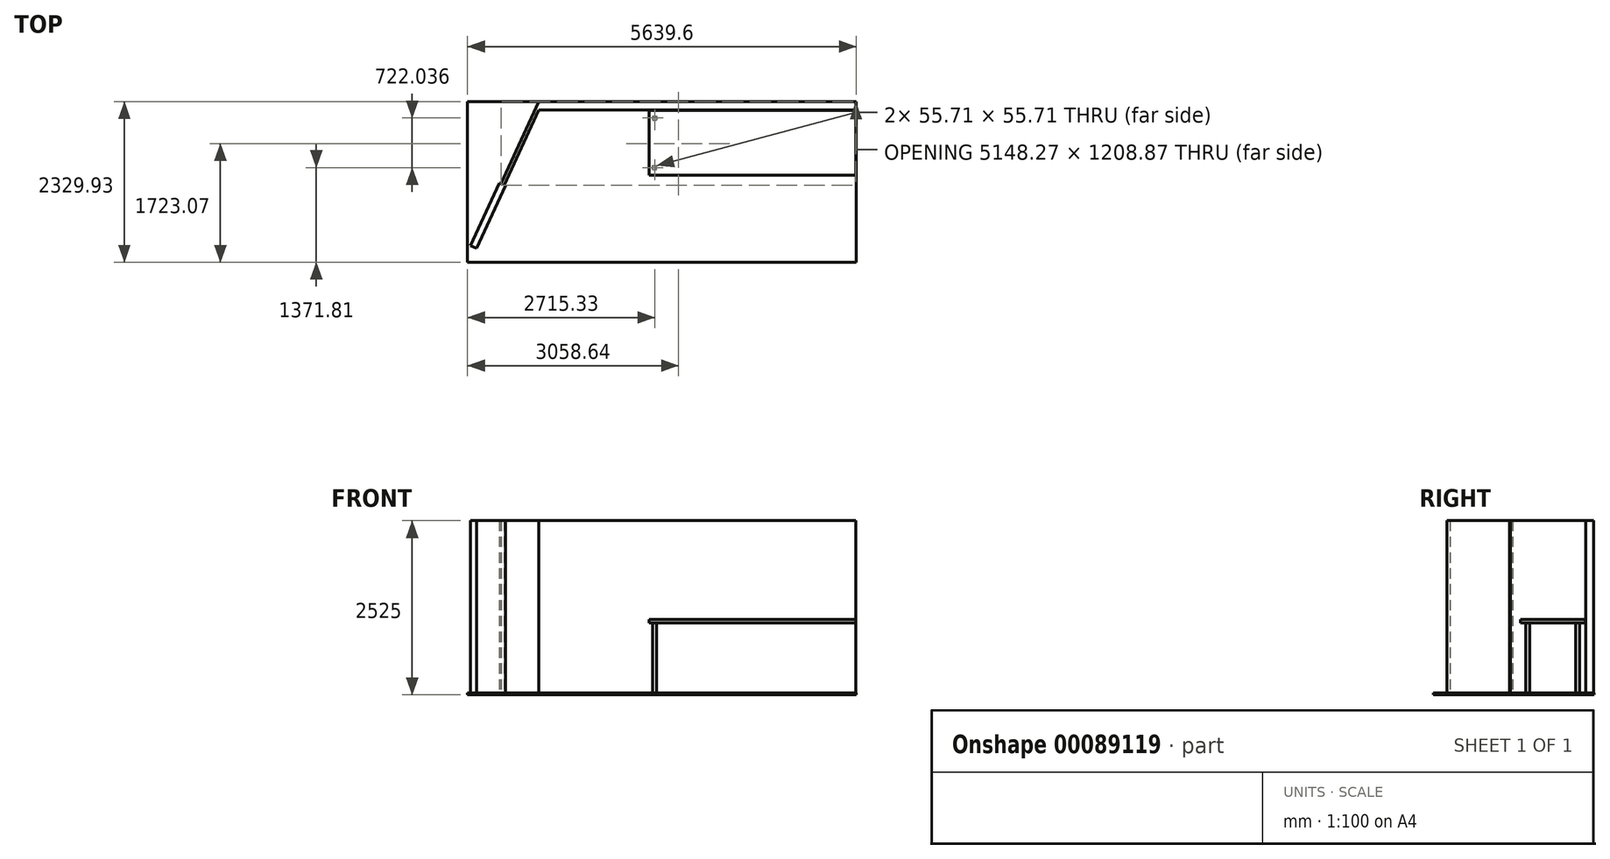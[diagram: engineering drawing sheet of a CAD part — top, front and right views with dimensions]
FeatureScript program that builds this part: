
annotation { "Feature Type Name" : "Feature", "Feature Type Description" : "" }
export const myFeature = defineFeature(function(context is Context, id is Id, definition is map)
    precondition{}
    {
        {
            var Q0;
            Q0=qCreatedBy(makeId("Top.planeOp"),FACE);
            var sketch = newSketch(context, id + "F0", { "sketchPlane" : qUnion([Q0])});
            skLineSegment(sketch, "E0.bottom", {"start": v(-637.71, 864.23) * mm, "end": v(2362.29, 864.23) * mm, "construction": true});
            skLineSegment(sketch, "E0.top", {"start": v(-637.71, -85.77) * mm, "end": v(2362.29, -85.77) * mm, "construction": true});
            skLineSegment(sketch, "E0.left", {"start": v(-637.71, 864.23) * mm, "end": v(-637.71, -85.77) * mm, "construction": true});
            skLineSegment(sketch, "E0.right", {"start": v(2362.29, 864.23) * mm, "end": v(2362.29, -85.77) * mm, "construction": true});
            skLineSegment(sketch, "E1", {"start": v(-637.71, 864.23) * mm, "end": v(-2237.71, 864.23) * mm});
            skLineSegment(sketch, "E2", {"start": v(-2237.71, 864.23) * mm, "end": v(-2740.58, -225.32) * mm});
            skLineSegment(sketch, "E3", {"start": v(-2740.58, -225.32) * mm, "end": v(-2785.98, -204.37) * mm});
            skLineSegment(sketch, "E4", {"start": v(-2785.98, -204.37) * mm, "end": v(-2237.71, 983.55) * mm});
            skLineSegment(sketch, "E5", {"start": v(-2237.71, 983.55) * mm, "end": v(2362.29, 983.55) * mm});
            skLineSegment(sketch, "E6", {"start": v(2362.29, 983.55) * mm, "end": v(2362.29, 864.23) * mm});
            skLineSegment(sketch, "E7", {"start": v(-2237.71, 864.23) * mm, "end": v(-2237.71, -45.77) * mm, "construction": true});
            skLineSegment(sketch, "E8", {"start": v(-2237.71, -45.77) * mm, "end": v(-2657.71, -45.77) * mm, "construction": true});
            skLineSegment(sketch, "E9", {"start": v(-2237.71, 864.23) * mm, "end": v(-2237.71, 1303.18) * mm, "construction": true});
            skLineSegment(sketch, "E10", {"start": v(-637.71, 864.23) * mm, "end": v(2362.29, 864.23) * mm});
            skLineSegment(sketch, "E11.bottom", {"start": v(-2740.58, -225.32) * mm, "end": v(-2808.68, -193.9) * mm});
            skLineSegment(sketch, "E11.top", {"start": v(-3136.94, -1143.76) * mm, "end": v(-3227.74, -1101.85) * mm});
            skLineSegment(sketch, "E11.left", {"start": v(-2717.88, -235.8) * mm, "end": v(-3136.94, -1143.76) * mm});
            skLineSegment(sketch, "E11.right", {"start": v(-2808.68, -193.9) * mm, "end": v(-3227.74, -1101.85) * mm});
            skLineSegment(sketch, "E12", {"start": v(-2740.58, -225.32) * mm, "end": v(-2717.88, -235.8) * mm});
            skSolve(sketch);
        }
        {
            var Q0;
            Q0=makeQuery(id+"F0.imprint","IMPRINT",FACE,{"disambiguationData":[TD([[makeQuery(id+"F0.imprint","IMPRINT",EDGE,{"derivedFrom":sQuery(id+"F0.wireOp",EDGE,"E1")}),-1.0]])]});
            var Q1;
            Q1=makeQuery(id+"F0.imprint","IMPRINT",FACE,{"disambiguationData":[TD([[makeQuery(id+"F0.imprint","IMPRINT",EDGE,{"derivedFrom":sQuery(id+"F0.wireOp",EDGE,"E11.top")}),-1.0]])]});
            extrude(context, id + "F1", {"entities" : qUnion([Q0, Q1]), "depth" : 2500 * mm});
        }
        {
            var Q0;
            Q0=makeQuery(id+"F1.opExtrude","CAP_FACE",FACE,{"disambiguationData":[OSD([sQuery(id+"F0.wireOp",EDGE,"E1"),sQuery(id+"F0.wireOp",EDGE,"E2"),sQuery(id+"F0.wireOp",EDGE,"E3"),sQuery(id+"F0.wireOp",EDGE,"E4"),sQuery(id+"F0.wireOp",EDGE,"E5"),sQuery(id+"F0.wireOp",EDGE,"E6"),sQuery(id+"F0.wireOp",EDGE,"E10")])],"isStart":true});
            cPlane(context, id + "F2", {"entities" : qUnion([Q0]), "cplaneType" : CPlaneType.OFFSET, "offset" : 1065 * mm, "oppositeDirection" : true, "width" : 150 * mm, "height" : 150 * mm});
        }
        {
            var Q0;
            Q0=qCreatedBy(id+"F2.planeOp",FACE);
            var sketch = newSketch(context, id + "F3", { "sketchPlane" : qUnion([Q0])});
            skLineSegment(sketch, "E13.bottom", {"start": v(-636.4, 81.22) * mm, "end": v(2359.83, 81.22) * mm});
            skLineSegment(sketch, "E13.top", {"start": v(-636.4, -858.96) * mm, "end": v(2359.83, -858.96) * mm});
            skLineSegment(sketch, "E13.left", {"start": v(-636.4, 81.22) * mm, "end": v(-636.4, -858.96) * mm});
            skLineSegment(sketch, "E13.right", {"start": v(2359.83, 81.22) * mm, "end": v(2359.83, -858.96) * mm});
            skSolve(sketch);
        }
        {
            var Q0;
            Q0=makeQuery(id+"F3.imprint","IMPRINT",FACE,{"disambiguationData":[TD([[makeQuery(id+"F3.imprint","IMPRINT",EDGE,{"derivedFrom":sQuery(id+"F3.wireOp",EDGE,"E13.bottom")}),-1.0]])]});
            extrude(context, id + "F4", {"entities" : qUnion([Q0]), "depth" : 45 * mm});
        }
        {
            var Q0;
            Q0=makeQuery(id+"F0.imprint","IMPRINT",FACE,{"disambiguationData":[TD([[makeQuery(id+"F0.imprint","IMPRINT",EDGE,{"derivedFrom":sQuery(id+"F0.wireOp",EDGE,"E1")}),-1.0]])]});
            var sketch = newSketch(context, id + "F5", { "sketchPlane" : qUnion([Q0])});
            skLineSegment(sketch, "E14.bottom", {"start": v(2369.1, 985.97) * mm, "end": v(-3270.49, 985.97) * mm});
            skLineSegment(sketch, "E14.top", {"start": v(2369.1, -1343.96) * mm, "end": v(-3270.49, -1343.96) * mm});
            skLineSegment(sketch, "E14.left", {"start": v(2369.1, 985.97) * mm, "end": v(2369.1, -1343.96) * mm});
            skLineSegment(sketch, "E14.right", {"start": v(-3270.49, 985.97) * mm, "end": v(-3270.49, -1343.96) * mm});
            skSolve(sketch);
        }
        {
            var Q0;
            Q0=makeQuery(id+"F5.imprint","IMPRINT",FACE,{"disambiguationData":[TD([[makeQuery(id+"F5.imprint","IMPRINT",EDGE,{"derivedFrom":sQuery(id+"F5.wireOp",EDGE,"E14.bottom")}),1.0]])]});
            extrude(context, id + "F6", {"entities" : qUnion([Q0]), "oppositeDirection" : true, "depth" : 25 * mm});
        }
        {
            var Q0;
            Q0=makeQuery(id+"F4.opExtrude","CAP_FACE",FACE,{"disambiguationData":[OSD([sQuery(id+"F3.wireOp",EDGE,"E13.bottom"),sQuery(id+"F3.wireOp",EDGE,"E13.top"),sQuery(id+"F3.wireOp",EDGE,"E13.left"),sQuery(id+"F3.wireOp",EDGE,"E13.right")])],"isStart":false});
            var sketch = newSketch(context, id + "F7", { "sketchPlane" : qUnion([Q0])});
            skLineSegment(sketch, "E15.bottom", {"start": v(-583.02, 0) * mm, "end": v(-527.3, 0) * mm});
            skLineSegment(sketch, "E15.top", {"start": v(-583.02, -55.7) * mm, "end": v(-527.3, -55.7) * mm});
            skLineSegment(sketch, "E15.left", {"start": v(-583.02, 0) * mm, "end": v(-583.02, -55.7) * mm});
            skLineSegment(sketch, "E15.right", {"start": v(-527.3, 0) * mm, "end": v(-527.3, -55.7) * mm});
            skLineSegment(sketch, "E16", {"start": v(-636.4, -388.87) * mm, "end": v(2359.83, -388.87) * mm, "construction": true});
            skLineSegment(sketch, "E17.MirrorCS", {"start": v(-583.02, -722.04) * mm, "end": v(-527.3, -722.04) * mm});
            skLineSegment(sketch, "E18.MirrorCS", {"start": v(-583.02, -777.74) * mm, "end": v(-583.02, -722.04) * mm});
            skLineSegment(sketch, "E19.MirrorCS", {"start": v(-583.02, -777.74) * mm, "end": v(-527.3, -777.74) * mm});
            skLineSegment(sketch, "E20.MirrorCS", {"start": v(-527.3, -777.74) * mm, "end": v(-527.3, -722.04) * mm});
            skSolve(sketch);
        }
        {
            var Q0;
            Q0 = qSketchRegion(id + "F7", true);
            var Q1;
            Q1=makeQuery(id+"F6.opExtrude","CAP_FACE",FACE,{"disambiguationData":[OSD([sQuery(id+"F0.wireOp",EDGE,"E1"),sQuery(id+"F0.wireOp",EDGE,"E2"),sQuery(id+"F0.wireOp",EDGE,"E3"),sQuery(id+"F0.wireOp",EDGE,"E4"),sQuery(id+"F0.wireOp",EDGE,"E5"),sQuery(id+"F0.wireOp",EDGE,"E6"),sQuery(id+"F0.wireOp",EDGE,"E10"),sQuery(id+"F5.wireOp",EDGE,"E14.bottom"),sQuery(id+"F5.wireOp",EDGE,"E14.top"),sQuery(id+"F5.wireOp",EDGE,"E14.left"),sQuery(id+"F5.wireOp",EDGE,"E14.right")])],"isStart":true});
            extrude(context, id + "F8", {"entities" : qUnion([Q0]), "operationType" : NewBodyOperationType.ADD, "endBound" : BoundingType.UP_TO_SURFACE, "endBoundEntityFace" : qUnion([Q1]), "depth" : 1000 * mm});
        }
    });
